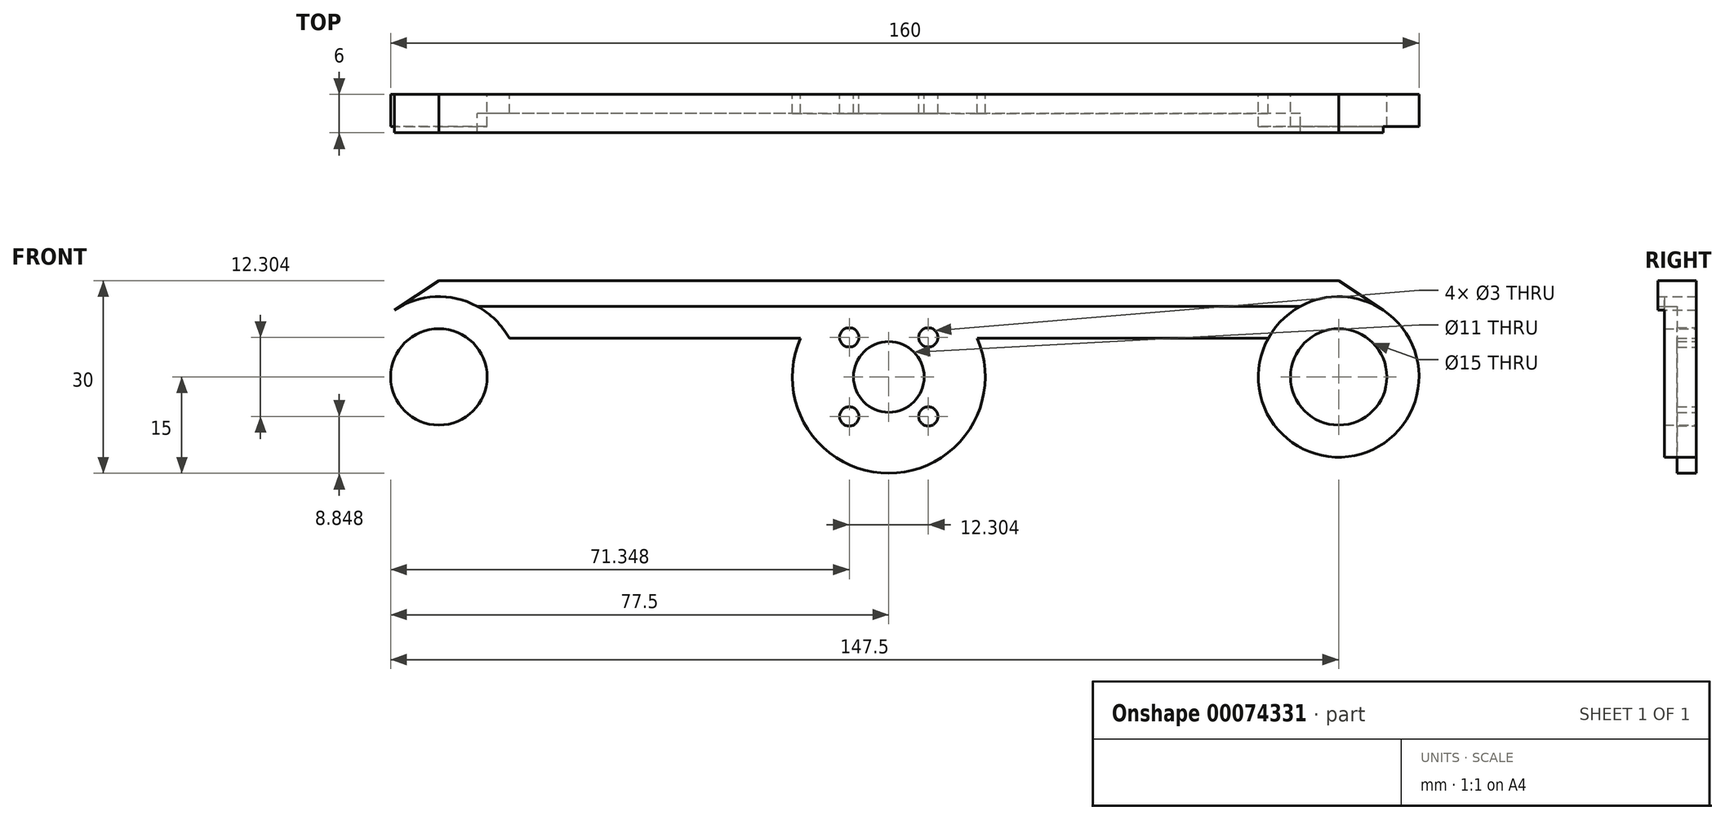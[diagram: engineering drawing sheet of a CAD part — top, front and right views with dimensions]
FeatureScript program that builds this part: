
annotation { "Feature Type Name" : "Feature", "Feature Type Description" : "" }
export const myFeature = defineFeature(function(context is Context, id is Id, definition is map)
    precondition{}
    {
        {
            var Q0;
            Q0=qCreatedBy(makeId("Front.planeOp"),FACE);
            var sketch = newSketch(context, id + "F0", { "sketchPlane" : qUnion([Q0])});
            skCircle(sketch, "E0", {"center": v(70, 0) * mm, "radius": 7.5 * mm});
            skCircle(sketch, "E1.MirrorC", {"center": v(-70, 0) * mm, "radius": 7.5 * mm});
            skCircle(sketch, "E2", {"center": v(70, 0) * mm, "radius": 12.5 * mm});
            skCircle(sketch, "E3", {"center": v(0, 0) * mm, "radius": 5.5 * mm});
            skCircle(sketch, "E4", {"center": v(6.15, -6.15) * mm, "radius": 1.5 * mm});
            skCircle(sketch, "E5", {"center": v(0, 0) * mm, "radius": 15 * mm});
            skLineSegment(sketch, "E6", {"start": v(13.75, 6) * mm, "end": v(59.03, 6) * mm});
            skLineSegment(sketch, "E7", {"start": v(0, 15) * mm, "end": v(70, 15) * mm});
            skLineSegment(sketch, "E8", {"start": v(70, 15) * mm, "end": v(76.9, 10.42) * mm});
            skLineSegment(sketch, "E9.MirrorCS", {"start": v(0, 15) * mm, "end": v(-70, 15) * mm});
            skLineSegment(sketch, "E10.MirrorCS", {"start": v(-13.75, 6) * mm, "end": v(-59.03, 6) * mm});
            skLineSegment(sketch, "E11.MirrorCS", {"start": v(-70, 15) * mm, "end": v(-76.9, 10.42) * mm});
            skCircle(sketch, "E12.MirrorC", {"center": v(-70, 0) * mm, "radius": 12.5 * mm});
            skLineSegment(sketch, "E13", {"start": v(0, 0) * mm, "end": v(14.7, -14.7) * mm, "construction": true});
            skCircle(sketch, "E14.1.0", {"center": v(6.15, 6.15) * mm, "radius": 1.5 * mm});
            skCircle(sketch, "E14.2.0", {"center": v(-6.15, 6.15) * mm, "radius": 1.5 * mm});
            skCircle(sketch, "E14.3.0", {"center": v(-6.15, -6.15) * mm, "radius": 1.5 * mm});
            skCircle(sketch, "E15", {"center": v(0, 0) * mm, "radius": 4 * mm});
            skSolve(sketch);
        }
        {
            var Q0;
            Q0=makeQuery(id+"F0.imprint","IMPRINT",FACE,{"disambiguationData":[TD([[makeQuery(id+"F0.imprint","IMPRINT",EDGE,{"derivedFrom":sQuery(id+"F0.wireOp",EDGE,"E3")}),-1.0]])]});
            var Q1;
            {var subQ1=sQuery(id+"F0.wireOp",EDGE,"E6");Q1=makeQuery(id+"F0.imprint","IMPRINT",FACE,{"disambiguationData":[TD([[makeQuery(id+"F0.imprint","IMPRINT",EDGE,{"derivedFrom":subQ1}),1.0]])]});}
            var Q2;
            {var subQ2=sQuery(id+"F0.wireOp",EDGE,"E9.MirrorCS");Q2=makeQuery(id+"F0.imprint","IMPRINT",FACE,{"disambiguationData":[TD([[makeQuery(id+"F0.imprint","IMPRINT",EDGE,{"derivedFrom":subQ2}),1.0]])]});}
            extrude(context, id + "F1", {"entities" : qUnion([Q0, Q1, Q2]), "depth" : 3 * mm});
        }
        {
            var Q0;
            Q0=makeQuery(id+"F0.imprint","IMPRINT",FACE,{"disambiguationData":[TD([[makeQuery(id+"F0.imprint","IMPRINT",EDGE,{"derivedFrom":sQuery(id+"F0.wireOp",EDGE,"E0")}),-1.0]])]});
            var Q1;
            Q1=makeQuery(id+"F0.imprint","IMPRINT",FACE,{"disambiguationData":[TD([[makeQuery(id+"F0.imprint","IMPRINT",EDGE,{"derivedFrom":sQuery(id+"F0.wireOp",EDGE,"E1.MirrorC")}),1.0]])]});
            extrude(context, id + "F2", {"entities" : qUnion([Q0, Q1]), "operationType" : NewBodyOperationType.ADD, "depth" : 5 * mm});
        }
        {
            var Q0;
            Q0=makeQuery(id+"F1.opExtrude","CAP_FACE",FACE,{"disambiguationData":[OSD([sQuery(id+"F0.wireOp",EDGE,"E2"),sQuery(id+"F0.wireOp",EDGE,"E3"),sQuery(id+"F0.wireOp",EDGE,"E4"),sQuery(id+"F0.wireOp",EDGE,"3c587e37-c579-42fa-a115-0e234746d365.1.0"),sQuery(id+"F0.wireOp",EDGE,"3c587e37-c579-42fa-a115-0e234746d365.2.0"),sQuery(id+"F0.wireOp",EDGE,"3c587e37-c579-42fa-a115-0e234746d365.3.0"),sQuery(id+"F0.wireOp",EDGE,"E5"),sQuery(id+"F0.wireOp",EDGE,"E6"),sQuery(id+"F0.wireOp",EDGE,"E7"),sQuery(id+"F0.wireOp",EDGE,"E8"),sQuery(id+"F0.wireOp",EDGE,"E9.MirrorCS"),sQuery(id+"F0.wireOp",EDGE,"E10.MirrorCS"),sQuery(id+"F0.wireOp",EDGE,"E11.MirrorCS"),sQuery(id+"F0.wireOp",EDGE,"E12.MirrorC")])],"isStart":false});
            var sketch = newSketch(context, id + "F3", { "sketchPlane" : qUnion([Q0])});
            skLineSegment(sketch, "E16", {"start": v(64.06, 11) * mm, "end": v(0, 11) * mm});
            skLineSegment(sketch, "E17.MirrorCS", {"start": v(-64.06, 11) * mm, "end": v(0, 11) * mm});
            skSolve(sketch);
        }
        {
            var Q0;
            {var subQ2=sQuery(id+"F3.wireOp",EDGE,"E16");Q0=makeQuery(id+"F3.imprint","IMPRINT",FACE,{"disambiguationData":[TD([[makeQuery(id+"F3.imprint","IMPRINT",EDGE,{"derivedFrom":subQ2}),-1.0]])]});}
            extrude(context, id + "F4", {"entities" : qUnion([Q0]), "operationType" : NewBodyOperationType.ADD, "depth" : 3 * mm});
        }
    });
